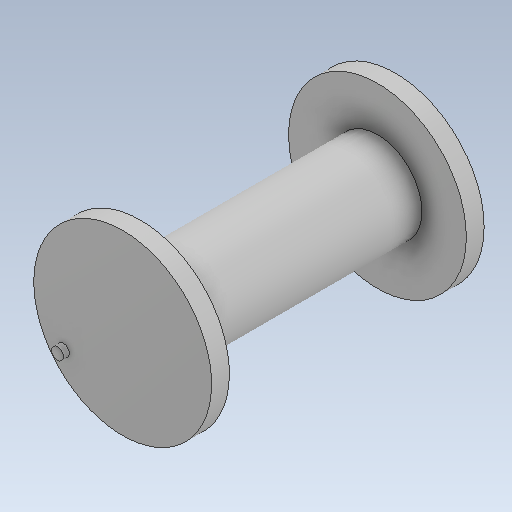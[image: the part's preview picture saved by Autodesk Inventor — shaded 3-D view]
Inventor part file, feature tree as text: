
AUTODESK INVENTOR PART (.ipt)
format: ipt  version: 2021.4 (Build 254397000, 397)  size: 121,856 bytes
history: imported  units: in
note: dims shown in document units (in); Inventor stores cm internally (conversion verified against a paired STEP export)
features: imported_body x1
ambient origin geometry x8: Origin, YZ Plane, XZ Plane, XY Plane, X Axis, Y Axis, Z Axis, Center Point
bodies: Solid1 (imported_parasolid), Solid2 (imported_parasolid), Body1 (imported_parasolid), Body2 (imported_parasolid)
feature tree (1):
  imported_body  NMx_Import_Brep_tag  [imported B-rep: ~10 faces, bbox_mm=[225.0, 215.0, 470.0]]
